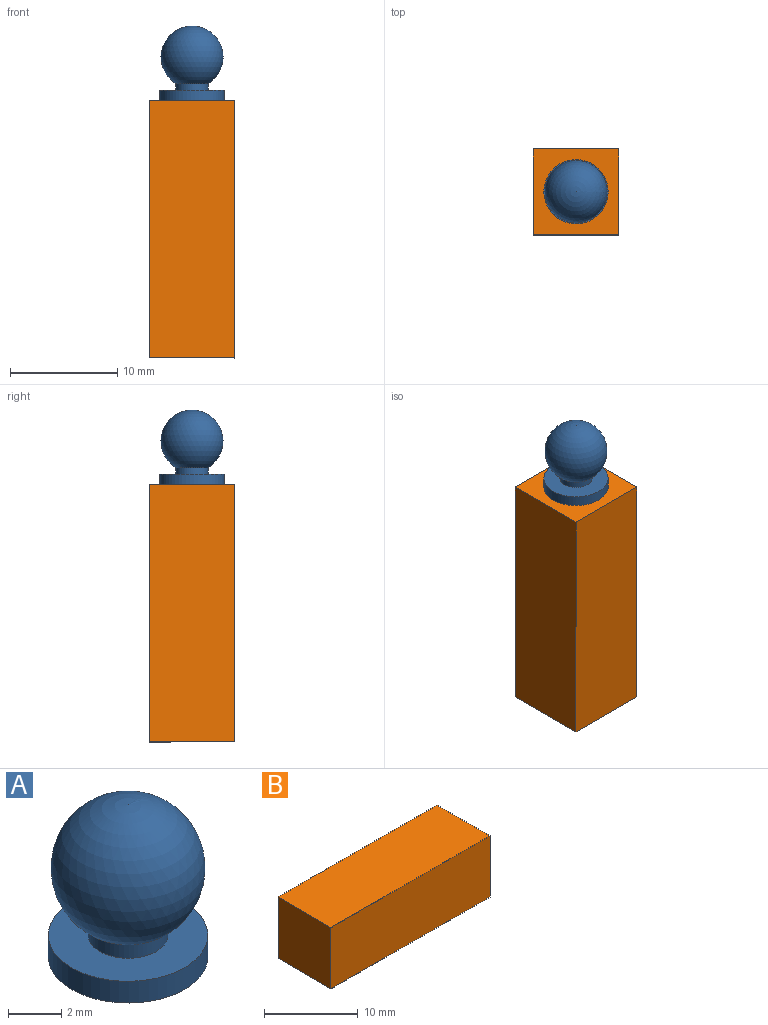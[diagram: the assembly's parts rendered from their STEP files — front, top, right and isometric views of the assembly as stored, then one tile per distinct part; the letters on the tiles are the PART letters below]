
ASSEMBLY  parts=2 mates=1
PART A: 5 faces, bbox 6x6x7 mm
  f0: plane 6x6mm, normal (0,0,-1), area 28.3mm2, adj f4
  f1: sphere r=2.9mm, area 98.1mm2, adj f2
  f2: cylinder r=1.5mm len=3mm, axis (0,0,1), area 5.8mm2, adj f1,f3
  f3: plane 6x6mm, normal (0,0,1), area 21.2mm2, adj f2,f4
  f4: cylinder r=3mm len=6mm, axis (0,0,1), area 18.8mm2, adj f0,f3
PART B: 6 faces, bbox 24x8x8 mm
  f0: plane 24x8mm, normal (0,0,-1), area 192mm2, adj f1,f3,f4,f5
  f1: plane 8x8mm, normal (1,0,0), area 64mm2, adj f0,f2,f4,f5
  f2: plane 24x8mm, normal (0,0,1), area 192mm2, adj f1,f3,f4,f5
  f3: plane 8x8mm, normal (-1,0,0), area 64mm2, adj f0,f2,f4,f5
  f4: plane 24x8mm, normal (0,-1,0), area 192mm2, adj f0,f1,f2,f3
  f5: plane 24x8mm, normal (0,1,0), area 192mm2, adj f0,f1,f2,f3
PLACE A t=(-3.2,-4.84,4.01)mm
PLACE B rot(axis=(0,1,0),90deg) t=(-7.2,-4.84,-7.99)mm
MATE fastened A.f2 <-> B.f3  axis (0,0,-1) through (-3.2,-4.84,4.01)mm
